# Revit family: Strong
name_source: partatom
category: Generic Models
units: mm (PartAtom-declared; Revit-internal decimal feet)

## family parameters
Always vertical = Yes
Can host rebar = No
Cut with Voids When Loaded = No
Host = Wall
Part Type = Normal
Room Calculation Point = No
Round Connector Dimension = Use Diameter
Shared = No

## types (18) — shared parameters
Manufacturer = Masterwatt B.V.
URL = https://masterwatt.nl
Voltage = 230 V
zero-valued in all types: Default Elevation

## per-type parameters (varying)
| type | Art. No. | Model | STG-B 350 | STG-B 351 | STG-B 450 | STG-B 501 | STG-B 651 | STG-B 750 | STG-B 851 | STG-B 950 | STG-W 350 | STG-W 351 | STG-W 450 | STG-W 501 | STG-W 651 | STG-W 750 | STG-W 851 | STG-W 950 | Watt |
| STG-W 351 | 880 110 350 | Infraroodpaneel STG-W 351 | No | No | No | No | No | No | No | No | No | Yes | No | No | No | No | No | No | 400 VA |
| STG-W 501 | 880 110 500 | Infraroodpaneel STG-W 501 | No | No | No | No | No | No | No | No | No | No | No | Yes | No | No | No | No | 500 VA |
| STG-W 651 | 880 110 650 | Infraroodpaneel STG-W 651 | No | No | No | No | No | No | No | No | No | No | No | No | Yes | No | No | No | 670 VA |
| STG-W 851 | 880 110 850 | Infraroodpaneel STG-W 851 | No | No | No | No | No | No | No | No | No | No | No | No | No | No | Yes | No | 820 VA |
| STG-W 350 | 880 100 350 | Infraroodpaneel STG-W 350 | No | No | No | No | No | No | No | No | Yes | No | No | No | No | No | No | No | 400 VA |
| STG-W 450 | 880 100 450 | Infraroodpaneel STG-W 450 | No | No | No | No | No | No | No | No | No | No | Yes | No | No | No | No | No | 500 VA |
| STG-W 750 | 880 100 750 | Infraroodpaneel STG-W 750 | No | No | No | No | No | No | No | No | No | No | No | No | No | Yes | No | No | 800 VA |
| STG-W 950 | 880 100 950 | Infraroodpaneel STG-W 950 | No | No | No | No | No | No | No | No | No | No | No | No | No | No | No | Yes | 1000 VA |
| STG-W 1200 | 880 100 120 | Infraroodpaneel STG-W 1200 | No | No | No | No | No | No | No | No | No | No | No | No | No | No | No | No | 1250 VA |
| STG-B 1200 | 880 100 121 | Infraroodpaneel STG-B 1200 | No | No | No | No | No | No | No | No | No | No | No | No | No | No | No | No | 1250 VA |
| STG-B 350 | 880 100 351 | Infraroodpaneel STG-B 350 | Yes | No | No | No | No | No | No | No | No | No | No | No | No | No | No | No | 400 VA |
| STG-B 351 | 880 110 351 | Infraroodpaneel STG-B 351 | No | Yes | No | No | No | No | No | No | No | No | No | No | No | No | No | No | 400 VA |
| STG-B 450 | 880 100 451 | Infraroodpaneel STG-B 450 | No | No | Yes | No | No | No | No | No | No | No | No | No | No | No | No | No | 500 VA |
| STG-B 501 | 880 110 501 | Infraroodpaneel STG-B 501 | No | No | No | Yes | No | No | No | No | No | No | No | Yes | No | No | No | No | 500 VA |
| STG-B- 651 | 880 110 651 | Infraroodpaneel STG-B 651 | No | No | No | No | Yes | No | No | No | No | No | No | No | No | No | No | No | 670 VA |
| STG-B 750 | 880 100 751 | Infraroodpaneel STG-B 750 | No | No | No | No | No | Yes | No | No | No | No | No | No | No | No | No | No | 800 VA |
| STG-B 851 | 880 110 851 | Infraroodpaneel STG-B 851 | No | No | No | No | No | No | Yes | No | No | No | No | No | No | No | No | No | 820 VA |
| STG-B 950 | 880 100 951 | Infraroodpaneel STG-B 950 | No | No | No | No | No | No | No | Yes | No | No | No | No | No | No | No | No | 1000 VA |

type visibility flags (boolean, named after types; folded from table):
- STG-W 351: Yes: (none)
- STG-W 501: Yes: (none)
- STG-W 651: Yes: (none)
- STG-W 851: Yes: (none)
- STG-W 350: Yes: (none)
- STG-W 450: Yes: (none)
- STG-W 750: Yes: (none)
- STG-W 950: Yes: (none)
- STG-W 1200: Yes: STG-W 1200
- STG-B 1200: Yes: STG-B 1200
- STG-B 350: Yes: (none)
- STG-B 351: Yes: (none)
- STG-B 450: Yes: (none)
- STG-B 501: Yes: (none)
- STG-B- 651: Yes: (none)
- STG-B 750: Yes: (none)
- STG-B 851: Yes: (none)
- STG-B 950: Yes: (none)

## geometry (parser evidence)
native form markers: Sweep x38
no freeform markers — native parametric forms only
